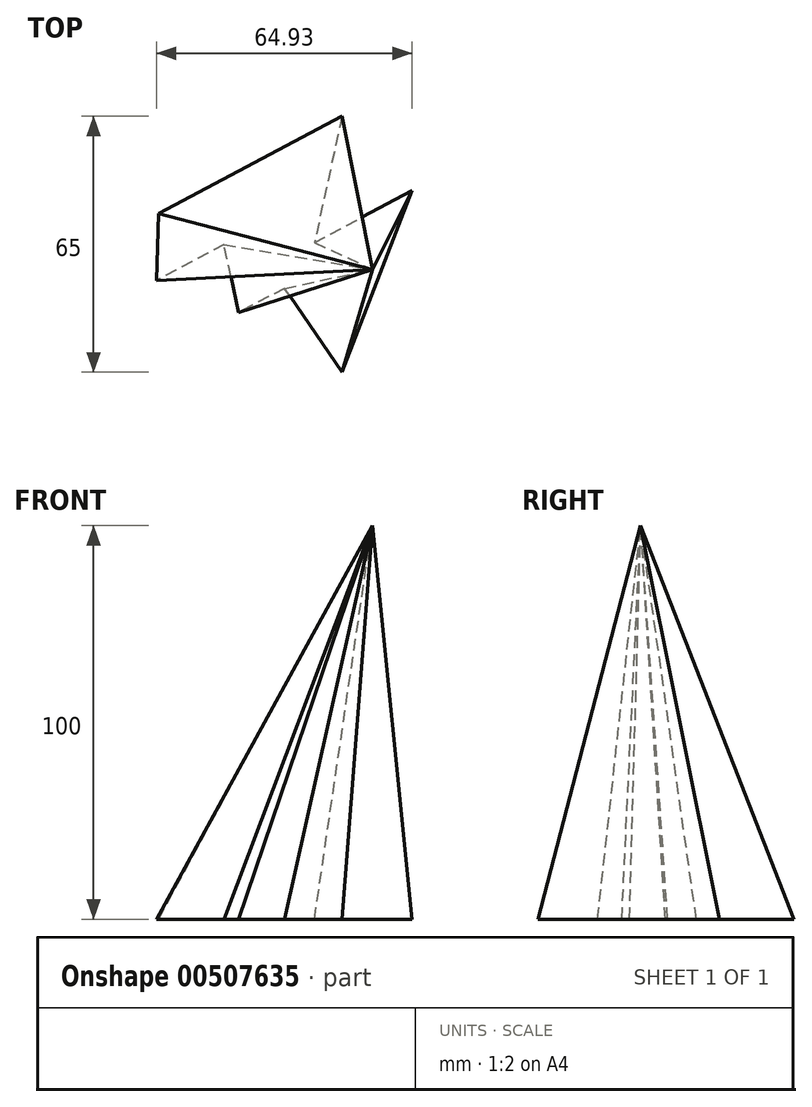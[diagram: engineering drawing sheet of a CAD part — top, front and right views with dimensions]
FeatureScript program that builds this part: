
annotation { "Feature Type Name" : "Feature", "Feature Type Description" : "" }
export const myFeature = defineFeature(function(context is Context, id is Id, definition is map)
    precondition{}
    {
        {
            var Q0;
            Q0=qCreatedBy(makeId("Top.planeOp"),FACE);
            var sketch = newSketch(context, id + "F0", { "sketchPlane" : qUnion([Q0])});
            skLineSegment(sketch, "E0", {"start": v(-46.64, 14.14) * mm, "end": v(0, 38.91) * mm});
            skLineSegment(sketch, "E1", {"start": v(0, 38.91) * mm, "end": v(-7, 6.85) * mm});
            skLineSegment(sketch, "E2", {"start": v(-7, 6.85) * mm, "end": v(17.8, 20.02) * mm});
            skLineSegment(sketch, "E3", {"start": v(17.8, 20.02) * mm, "end": v(0, -26.09) * mm});
            skLineSegment(sketch, "E4", {"start": v(0, -26.09) * mm, "end": v(-14.57, -4.8) * mm});
            skLineSegment(sketch, "E5", {"start": v(-14.57, -4.8) * mm, "end": v(-26.23, -10.93) * mm});
            skLineSegment(sketch, "E6", {"start": v(-26.23, -10.93) * mm, "end": v(-30.02, 6.27) * mm});
            skLineSegment(sketch, "E7", {"start": v(-30.02, 6.27) * mm, "end": v(-47.13, -2.82) * mm});
            skLineSegment(sketch, "E8", {"start": v(-47.13, -2.82) * mm, "end": v(-46.64, 14.14) * mm});
            skSolve(sketch);
        }
        {
            var Q0;
            Q0=qCreatedBy(makeId("Top.planeOp"),FACE);
            cPlane(context, id + "F1", {"entities" : qUnion([Q0]), "cplaneType" : CPlaneType.OFFSET, "offset" : 100 * mm, "width" : 152.4 * mm, "height" : 152.4 * mm});
        }
        {
            var Q0;
            Q0=qCreatedBy(id+"F1.planeOp",FACE);
            var sketch = newSketch(context, id + "F2", { "sketchPlane" : qUnion([Q0])});
            skPoint(sketch, "E9", {"position": v(7.7, 0) * mm});
            skSolve(sketch);
        }
        {
            var Q0;
            Q0=makeQuery(id+"F0.imprint","IMPRINT",FACE,{"disambiguationData":[TD([[makeQuery(id+"F0.imprint","IMPRINT",EDGE,{"derivedFrom":sQuery(id+"F0.wireOp",EDGE,"E0")}),-1.0]])]});
            var Q1;
            Q1=sQuery(id+"F2.wireOp",VERTEX,"E9");
            loft(context, id + "F3", {"sheetProfilesArray" : [{ "sheetProfileEntities" : qUnion([Q0]) }, { "sheetProfileEntities" : qUnion([Q1]) }]});
        }
    });
